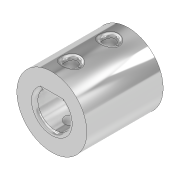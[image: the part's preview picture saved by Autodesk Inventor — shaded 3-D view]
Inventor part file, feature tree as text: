
AUTODESK INVENTOR PART (.ipt)
format: ipt  version: 2020 (Build 240168000, 168)  size: 242,688 bytes
history: native  units: in
note: dims shown in document units (in); Inventor stores cm internally (conversion verified against a paired STEP export)
features: extrude x2, fillet x1, sketch x1, projected_geometry x1
ambient origin geometry x8: Origin, YZ Plane, XZ Plane, XY Plane, X Axis, Y Axis, Z Axis, Center Point
bodies: Solid1 (feature_tree)
feature tree (5):
  extrude  "Extrusion1"  Depth=0.315in
  extrude  "Extrusion3"  Depth=0.4724in TaperAngle=0.0deg
  fillet  "Fillet2"  Radius=0.1181in
  sketch  "Sketch3"  dims[d0=0.1969in d1=0.315in d2=0.4724in d3=0.0in d17=0.1181in d18=0.1969in d19=0.0787in d20=0.0079in d21=0.0748in d22=0.0748in d23=0.3in d24=0.0in d25=0.0197in]
  projected_geometry  "Projected Loop1"
